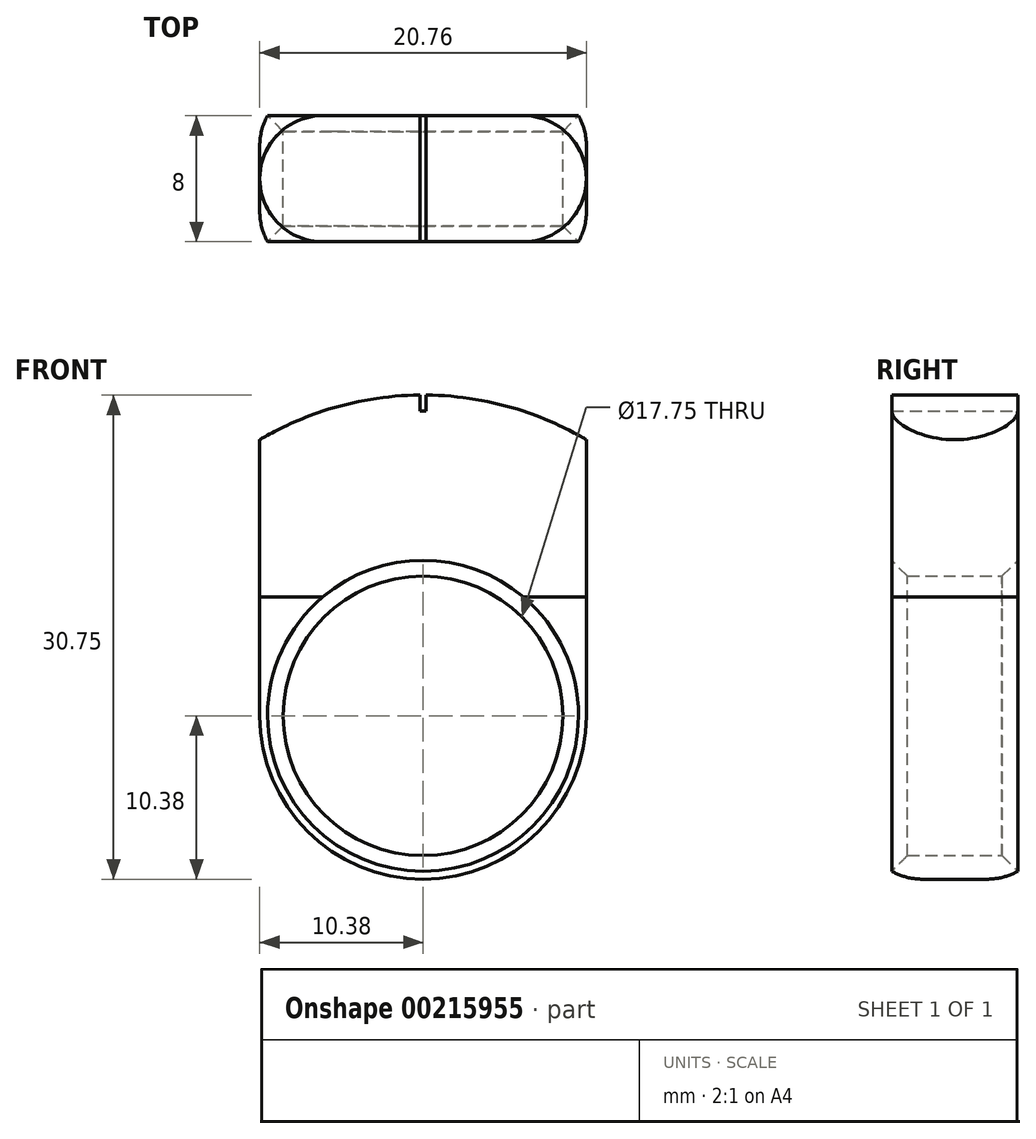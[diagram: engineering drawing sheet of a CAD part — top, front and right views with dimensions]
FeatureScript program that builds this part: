
annotation { "Feature Type Name" : "Feature", "Feature Type Description" : "" }
export const myFeature = defineFeature(function(context is Context, id is Id, definition is map)
    precondition{}
    {
        {
            var Q0;
            Q0=qCreatedBy(makeId("Front.planeOp"),FACE);
            var sketch = newSketch(context, id + "F0", { "sketchPlane" : qUnion([Q0])});
            skCircle(sketch, "E0", {"center": v(0, 0) * mm, "radius": 8.88 * mm});
            skCircle(sketch, "E1.0", {"center": v(0, 0) * mm, "radius": 10.38 * mm});
            skCircle(sketch, "E2.0", {"center": v(0, 0) * mm, "radius": 20.38 * mm});
            skLineSegment(sketch, "E3", {"start": v(10.38, 0) * mm, "end": v(10.38, 17.54) * mm});
            skLineSegment(sketch, "E4.MirrorCS", {"start": v(-10.38, 0) * mm, "end": v(-10.38, 17.54) * mm});
            skCircle(sketch, "E5.0", {"center": v(0, 0) * mm, "radius": 19.38 * mm});
            skLineSegment(sketch, "E6", {"start": v(-0.2, 20.37) * mm, "end": v(-0.2, 19.37) * mm});
            skLineSegment(sketch, "E7.MirrorCS", {"start": v(0.2, 20.37) * mm, "end": v(0.2, 19.37) * mm});
            skSolve(sketch);
        }
        {
            var Q0;
            Q0=makeQuery(id+"F0.imprint","IMPRINT",FACE,{"disambiguationData":[TD([[makeQuery(id+"F0.imprint","IMPRINT",EDGE,{"derivedFrom":sQuery(id+"F0.wireOp",EDGE,"E0")}),-1.0]])]});
            extrude(context, id + "F1", {"entities" : qUnion([Q0]), "depth" : 4 * mm, "hasSecondDirection" : true, "secondDirectionOppositeDirection" : true, "secondDirectionDepth" : 4 * mm});
        }
        {
            var Q0;
            Q0=makeQuery(id+"F1.opExtrude","CAP_EDGE",EDGE,{"disambiguationData":[OSD([sQuery(id+"F0.wireOp",EDGE,"E0")])],"isStart":false});
            var Q1;
            Q1=makeQuery(id+"F1.opExtrude","CAP_EDGE",EDGE,{"disambiguationData":[OSD([sQuery(id+"F0.wireOp",EDGE,"E0")])],"isStart":true});
            chamfer(context, id + "F2", {"entities" : qUnion([Q0, Q1]), "width" : 1 * mm, "tangentPropagation" : true});
        }
        {
            var Q0;
            {var subQ0=sQuery(id+"F0.wireOp",EDGE,"E3");var subQ1=sQuery(id+"F0.wireOp",EDGE,"E1.0");var subQ2=makeQuery(id+"F0.imprint","INTERSECT",VERTEX,{"derivedFrom":[subQ1,subQ0]});Q0=makeQuery(id+"F0.imprint","IMPRINT",FACE,{"disambiguationData":[TD([[makeQuery(id+"F0.imprint","IMPRINT",EDGE,{"disambiguationData":[TD([[subQ2,-1.0]])],"derivedFrom":subQ1}),-1.0]])]});}
            var Q1;
            {var subQ0=sQuery(id+"F0.wireOp",EDGE,"E3");var subQ1=sQuery(id+"F0.wireOp",EDGE,"E2.0");var subQ2=makeQuery(id+"F0.imprint","INTERSECT",VERTEX,{"derivedFrom":[subQ1,subQ0]});Q1=makeQuery(id+"F0.imprint","IMPRINT",FACE,{"disambiguationData":[TD([[makeQuery(id+"F0.imprint","IMPRINT",EDGE,{"disambiguationData":[TD([[subQ2,-1.0]])],"derivedFrom":subQ1}),1.0]])]});}
            var Q2;
            {var subQ3=sQuery(id+"F0.wireOp",EDGE,"E6");Q2=makeQuery(id+"F0.imprint","IMPRINT",FACE,{"disambiguationData":[TD([[makeQuery(id+"F0.imprint","IMPRINT",EDGE,{"derivedFrom":subQ3}),-1.0]])]});}
            extrude(context, id + "F3", {"entities" : qUnion([Q0, Q1, Q2]), "operationType" : NewBodyOperationType.ADD, "depth" : 4 * mm, "hasSecondDirection" : true, "secondDirectionOppositeDirection" : true, "secondDirectionDepth" : 4 * mm});
        }
        {
            var Q0;
            Q0=makeQuery(id+"F3.opExtrude","CAP_EDGE",EDGE,{"disambiguationData":[OSD([sQuery(id+"F0.wireOp",EDGE,"E3")])],"isStart":false});
            var Q1;
            Q1=makeQuery(id+"F3.opExtrude","CAP_EDGE",EDGE,{"disambiguationData":[OSD([sQuery(id+"F0.wireOp",EDGE,"E3")])],"isStart":true});
            var Q2;
            Q2=makeQuery(id+"F3.opExtrude","CAP_EDGE",EDGE,{"disambiguationData":[OSD([sQuery(id+"F0.wireOp",EDGE,"E4.MirrorCS")])],"isStart":false});
            var Q3;
            Q3=makeQuery(id+"F3.opExtrude","CAP_EDGE",EDGE,{"disambiguationData":[OSD([sQuery(id+"F0.wireOp",EDGE,"E4.MirrorCS")])],"isStart":true});
            fillet(context, id + "F4", {"entities" : qUnion([Q0, Q1, Q2, Q3]), "radius" : 4 * mm, "tangentPropagation" : true, "allowEdgeOverflow" : false});
        }
    });
